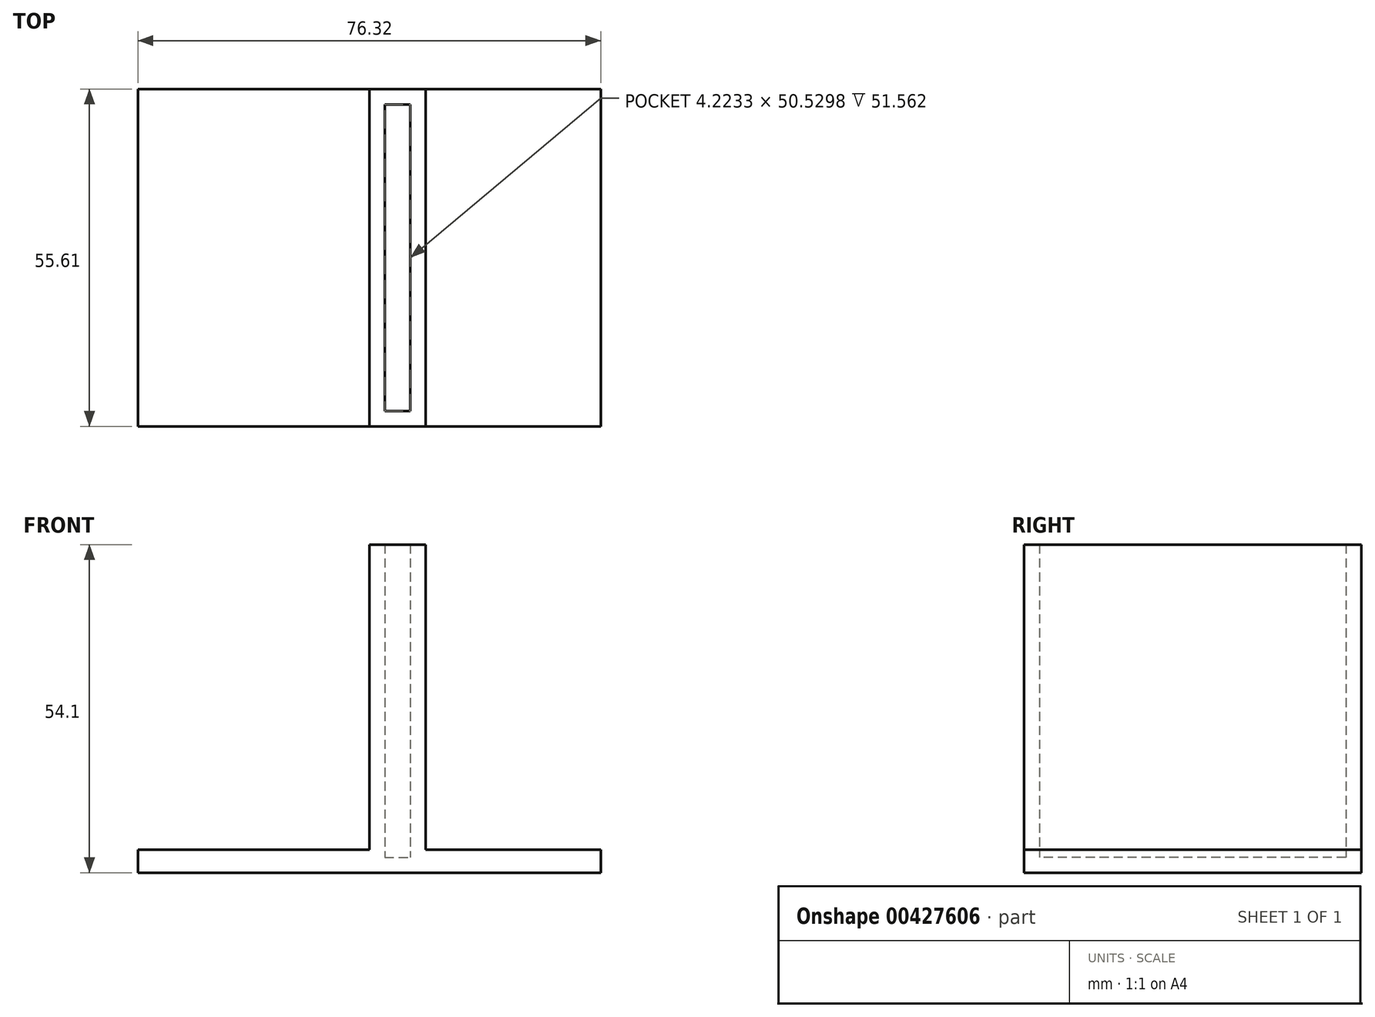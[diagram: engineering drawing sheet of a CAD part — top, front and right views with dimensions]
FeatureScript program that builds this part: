
annotation { "Feature Type Name" : "Feature", "Feature Type Description" : "" }
export const myFeature = defineFeature(function(context is Context, id is Id, definition is map)
    precondition{}
    {
        {
            var Q0;
            Q0=qCreatedBy(makeId("Top.planeOp"),FACE);
            var sketch = newSketch(context, id + "F0", { "sketchPlane" : qUnion([Q0])});
            skLineSegment(sketch, "E0.bottom", {"start": v(0, 0) * mm, "end": v(76.32, 0) * mm});
            skLineSegment(sketch, "E0.top", {"start": v(0, -55.6) * mm, "end": v(76.32, -55.6) * mm});
            skLineSegment(sketch, "E0.left", {"start": v(0, 0) * mm, "end": v(0, -55.6) * mm});
            skLineSegment(sketch, "E0.right", {"start": v(76.32, 0) * mm, "end": v(76.32, -55.6) * mm});
            skSolve(sketch);
        }
        {
            var Q0;
            Q0=makeQuery(id+"F0.imprint","IMPRINT",FACE,{"disambiguationData":[TD([[makeQuery(id+"F0.imprint","IMPRINT",EDGE,{"derivedFrom":sQuery(id+"F0.wireOp",EDGE,"E0.bottom")}),-1.0]])]});
            extrude(context, id + "F1", {"entities" : qUnion([Q0]), "depth" : 3.8 * mm});
        }
        {
            var Q0;
            Q0=makeQuery(id+"F1.opExtrude","CAP_FACE",FACE,{"disambiguationData":[OSD([sQuery(id+"F0.wireOp",EDGE,"E0.bottom"),sQuery(id+"F0.wireOp",EDGE,"E0.top"),sQuery(id+"F0.wireOp",EDGE,"E0.left"),sQuery(id+"F0.wireOp",EDGE,"E0.right")])],"isStart":false});
            var sketch = newSketch(context, id + "F2", { "sketchPlane" : qUnion([Q0])});
            skLineSegment(sketch, "E1.bottom", {"start": v(38.16, 0) * mm, "end": v(47.46, 0) * mm});
            skLineSegment(sketch, "E1.top", {"start": v(38.16, -55.6) * mm, "end": v(47.46, -55.6) * mm});
            skLineSegment(sketch, "E1.left", {"start": v(38.16, 0) * mm, "end": v(38.16, -55.6) * mm});
            skLineSegment(sketch, "E1.right", {"start": v(47.46, 0) * mm, "end": v(47.46, -55.6) * mm});
            skSolve(sketch);
        }
        {
            var Q0;
            Q0=makeQuery(id+"F2.imprint","IMPRINT",FACE,{"disambiguationData":[TD([[makeQuery(id+"F2.imprint","IMPRINT",EDGE,{"derivedFrom":sQuery(id+"F2.wireOp",EDGE,"E1.bottom")}),-1.0]])]});
            extrude(context, id + "F3", {"entities" : qUnion([Q0]), "operationType" : NewBodyOperationType.ADD, "depth" : 50.3 * mm});
        }
        {
            var Q0;
            Q0=makeQuery(id+"F3.opExtrude","CAP_FACE",FACE,{"disambiguationData":[OSD([sQuery(id+"F2.wireOp",EDGE,"E1.bottom"),sQuery(id+"F2.wireOp",EDGE,"E1.top"),sQuery(id+"F2.wireOp",EDGE,"E1.left"),sQuery(id+"F2.wireOp",EDGE,"E1.right")])],"isStart":false});
            shell(context, id + "F4", {"entities" : qUnion([Q0]), "thickness" : 2.54 * mm});
        }
    });
